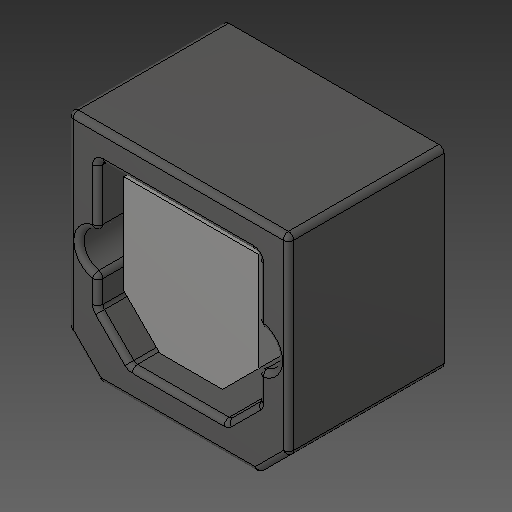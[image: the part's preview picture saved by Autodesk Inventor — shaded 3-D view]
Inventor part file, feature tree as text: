
AUTODESK INVENTOR PART (.ipt)
format: ipt  version: 2018.2 (Build 222227000, 227)  size: 159,232 bytes
history: native  units: mm
features: other x3, fillet x1
ambient origin geometry x8: Origin, YZ Plane, XZ Plane, XY Plane, X Axis, Y Axis, Z Axis, Center Point
bodies: Body1 (feature_tree), Body2 (feature_tree)
feature tree (4):
  other  "ソリッド1"
  other  "ソリッド2"
  fillet  "Fillet1"  [1 undecoded]
  other  "Boss-Extrude3"
note: 1 required parameter value undecoded (feature->parameter linkage not recoverable at this tier; creation-order binding heuristic only, values carry confidence <= 0.55)
